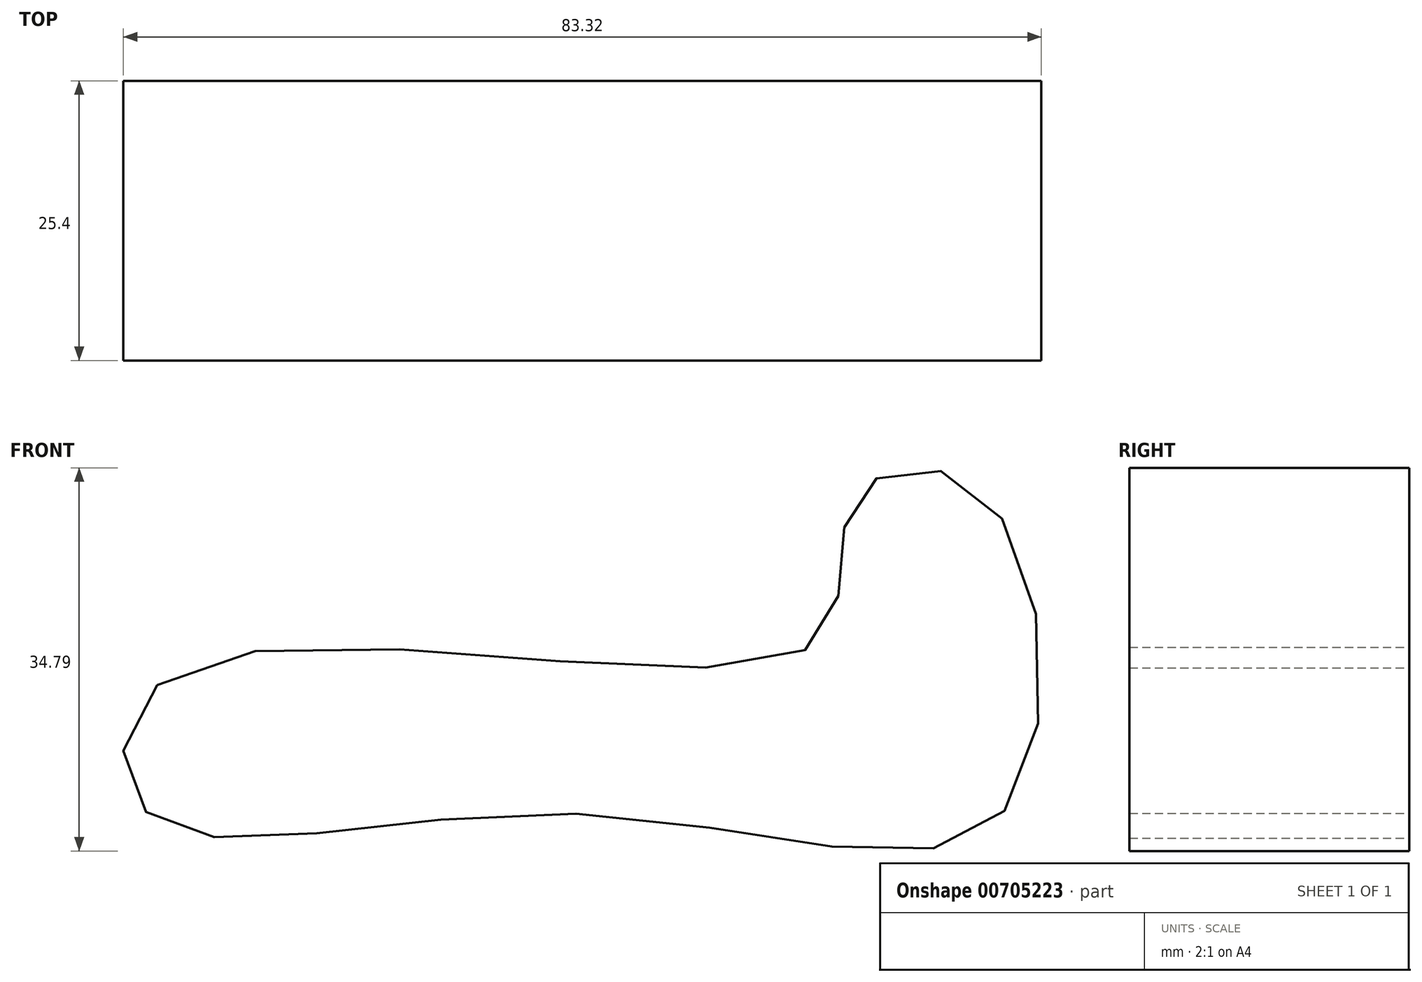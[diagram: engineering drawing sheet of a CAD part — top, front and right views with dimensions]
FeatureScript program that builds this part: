
annotation { "Feature Type Name" : "Feature", "Feature Type Description" : "" }
export const myFeature = defineFeature(function(context is Context, id is Id, definition is map)
    precondition{}
    {
        {
            var Q0;
            Q0=qCreatedBy(makeId("Front.planeOp"),FACE);
            var sketch = newSketch(context, id + "F0", { "sketchPlane" : qUnion([Q0])});
            skFitSpline(sketch, "E0", {"points": [v(0, 0) * mm, v(-38.86, 0) * mm, v(-36.19, 12.89) * mm, v(21.3, 15.18) * mm, v(25.11, 28.36) * mm, v(36.76, 29.12) * mm, v(38.67, 0) * mm, v(0, 0) * mm]});
            skSolve(sketch);
        }
        {
            var Q0;
            Q0 = qSketchRegion(id + "F0", true);
            extrude(context, id + "F1", {"entities" : qUnion([Q0]), "depth" : 25.4 * mm, "offsetDistance" : 25.4 * mm});
        }
    });
